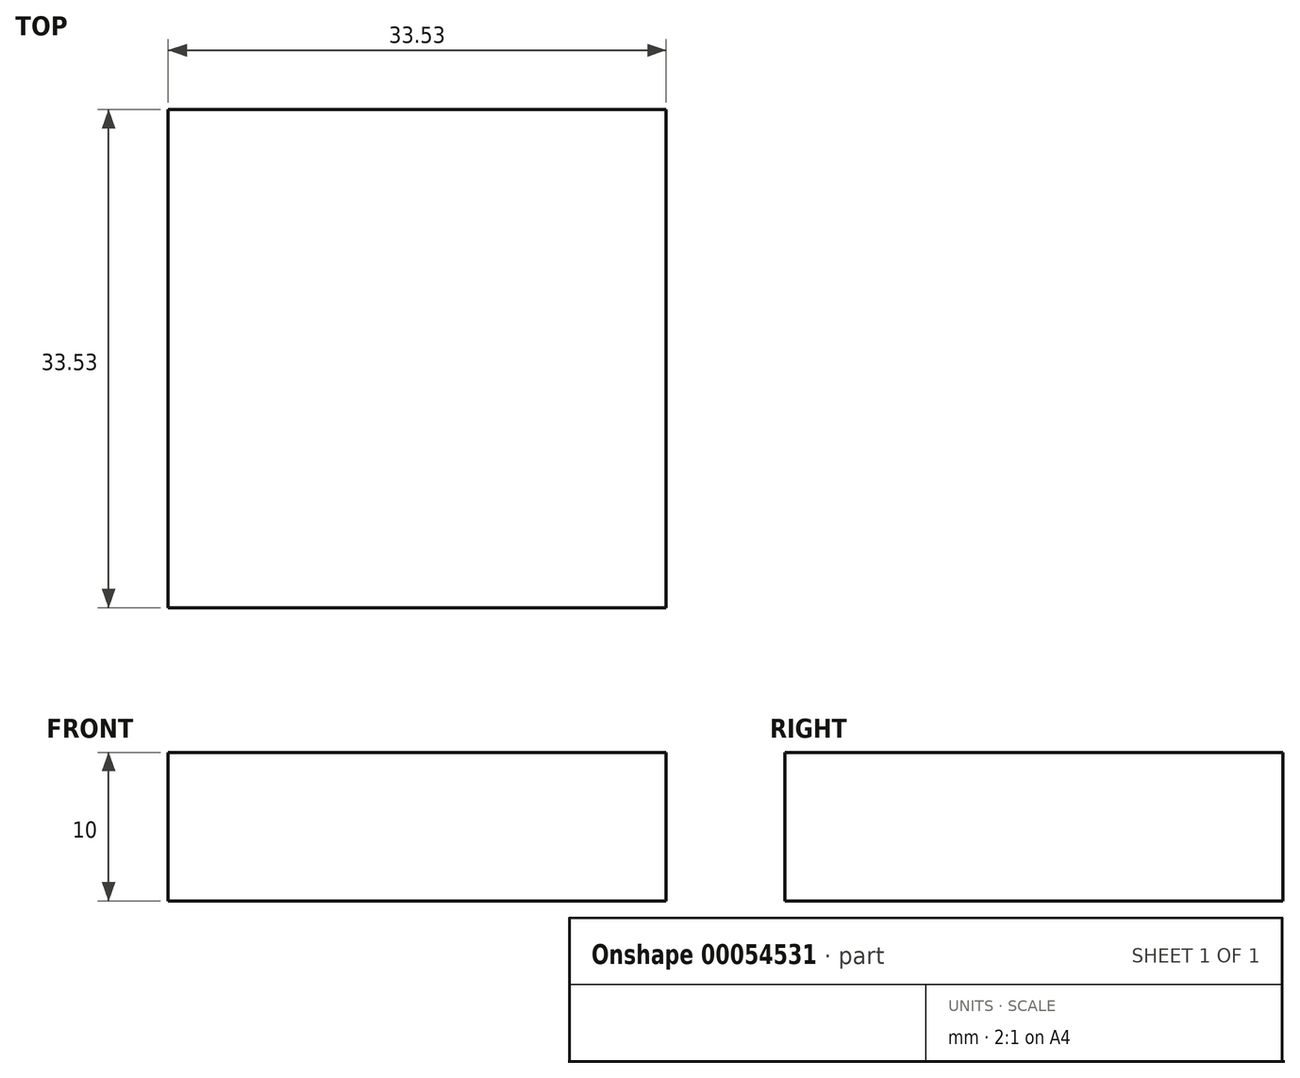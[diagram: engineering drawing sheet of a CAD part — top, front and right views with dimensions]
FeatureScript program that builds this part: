
annotation { "Feature Type Name" : "Feature", "Feature Type Description" : "" }
export const myFeature = defineFeature(function(context is Context, id is Id, definition is map)
    precondition{}
    {
        {
            var Q0;
            Q0=qCreatedBy(makeId("Top.planeOp"),FACE);
            var sketch = newSketch(context, id + "F0", { "sketchPlane" : qUnion([Q0])});
            skLineSegment(sketch, "E0.bottom", {"start": v(0, 0) * mm, "end": v(33.53, 0) * mm});
            skLineSegment(sketch, "E0.top", {"start": v(0, 33.53) * mm, "end": v(33.53, 33.53) * mm});
            skLineSegment(sketch, "E0.left", {"start": v(0, 0) * mm, "end": v(0, 33.53) * mm});
            skLineSegment(sketch, "E0.right", {"start": v(33.53, 0) * mm, "end": v(33.53, 33.53) * mm});
            skSolve(sketch);
        }
        {
            var Q0;
            Q0=makeQuery(id+"F0.imprint","IMPRINT",FACE,{"disambiguationData":[TD([[makeQuery(id+"F0.imprint","IMPRINT",EDGE,{"derivedFrom":sQuery(id+"F0.wireOp",EDGE,"E0.bottom")}),1.0]])]});
            extrude(context, id + "F1", {"entities" : qUnion([Q0]), "depth" : 10 * mm});
        }
    });
